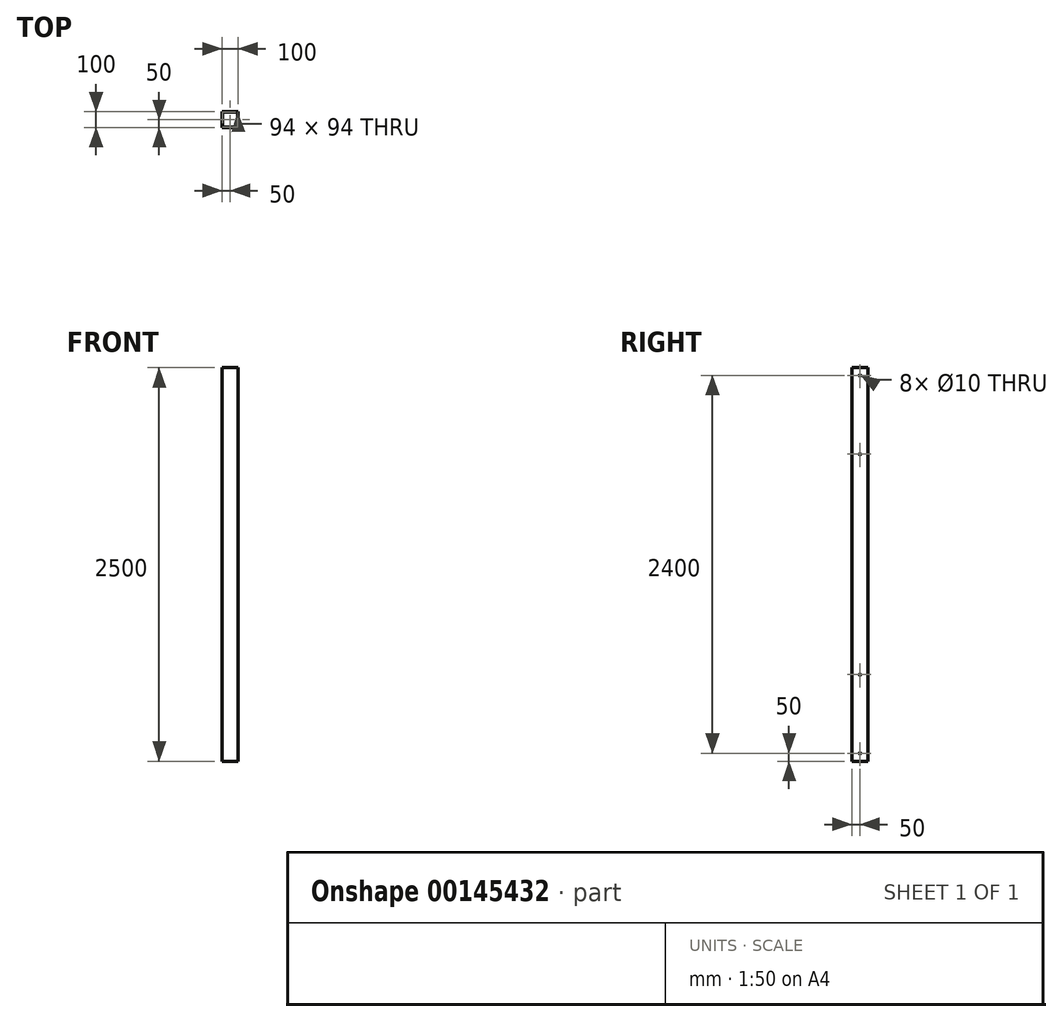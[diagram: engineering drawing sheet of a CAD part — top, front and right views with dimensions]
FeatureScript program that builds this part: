
annotation { "Feature Type Name" : "Feature", "Feature Type Description" : "" }
export const myFeature = defineFeature(function(context is Context, id is Id, definition is map)
    precondition{}
    {
        {
            var Q0;
            Q0=qCreatedBy(makeId("Top.planeOp"),FACE);
            var sketch = newSketch(context, id + "F0", { "sketchPlane" : qUnion([Q0])});
            skLineSegment(sketch, "E0.bottom", {"start": v(50, 50) * mm, "end": v(-50, 50) * mm});
            skLineSegment(sketch, "E0.top", {"start": v(50, -50) * mm, "end": v(-50, -50) * mm});
            skLineSegment(sketch, "E0.left", {"start": v(50, 50) * mm, "end": v(50, -50) * mm});
            skLineSegment(sketch, "E0.right", {"start": v(-50, 50) * mm, "end": v(-50, -50) * mm});
            skPoint(sketch, "E0.middle", {"position": v(0, 0) * mm});
            skLineSegment(sketch, "E1.0", {"start": v(47, 47) * mm, "end": v(-47, 47) * mm});
            skLineSegment(sketch, "E1.1", {"start": v(47, 47) * mm, "end": v(47, -47) * mm});
            skLineSegment(sketch, "E1.2", {"start": v(47, -47) * mm, "end": v(-47, -47) * mm});
            skLineSegment(sketch, "E1.3", {"start": v(-47, 47) * mm, "end": v(-47, -47) * mm});
            skSolve(sketch);
        }
        {
            var Q0;
            Q0 = qSketchRegion(id + "F0", true);
            extrude(context, id + "F1", {"entities" : qUnion([Q0]), "depth" : 2500 * mm, "symmetric" : true});
        }
        {
            var Q0;
            Q0=makeQuery(id+"F1.opExtrude","SWEPT_FACE",FACE,{"disambiguationData":[OSD([sQuery(id+"F0.wireOp",EDGE,"E0.left")])]});
            var sketch = newSketch(context, id + "F2", { "sketchPlane" : qUnion([Q0])});
            skCircle(sketch, "E2", {"center": v(0, 1200) * mm, "radius": 5 * mm});
            skCircle(sketch, "E3", {"center": v(0, 700) * mm, "radius": 5 * mm});
            skCircle(sketch, "E4.MirrorC", {"center": v(0, -700) * mm, "radius": 5 * mm});
            skCircle(sketch, "E5.MirrorC", {"center": v(0, -1200) * mm, "radius": 5 * mm});
            skSolve(sketch);
        }
        {
            var Q0;
            Q0 = qSketchRegion(id + "F2", true);
            extrude(context, id + "F3", {"entities" : qUnion([Q0]), "operationType" : NewBodyOperationType.REMOVE, "oppositeDirection" : true, "depth" : 300 * mm});
        }
    });
